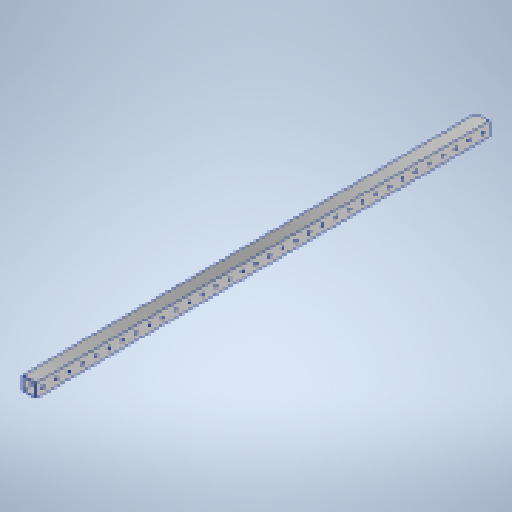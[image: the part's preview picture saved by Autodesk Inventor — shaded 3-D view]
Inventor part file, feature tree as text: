
AUTODESK INVENTOR PART (.ipt)
format: ipt  version: 2024 (Build 280153000, 153)  size: 320,512 bytes
history: native  units: in
note: dims shown in document units (in); Inventor stores cm internally (conversion verified against a paired STEP export)
features: extrude x2, sketch x1
ambient origin geometry x8: Origin, YZ Plane, XZ Plane, XY Plane, X Axis, Y Axis, Z Axis, Center Point
bodies: Solid1 (feature_tree)
feature tree (3):
  extrude  "Extrusion1"  Depth=1.0in
  extrude  "Extrusion2"  Depth=0.09in
  sketch  "Sketch2"  dims[d0=1.0in d1=1.0in d2=0.09in d3=34.0in d4=0.0in d5=0.201in d6=0.5in d7=0.5in d8=13.3858in d10=1.0in d11=0.3937in d13=1.0in d15=0.0in d16=0.0in]
